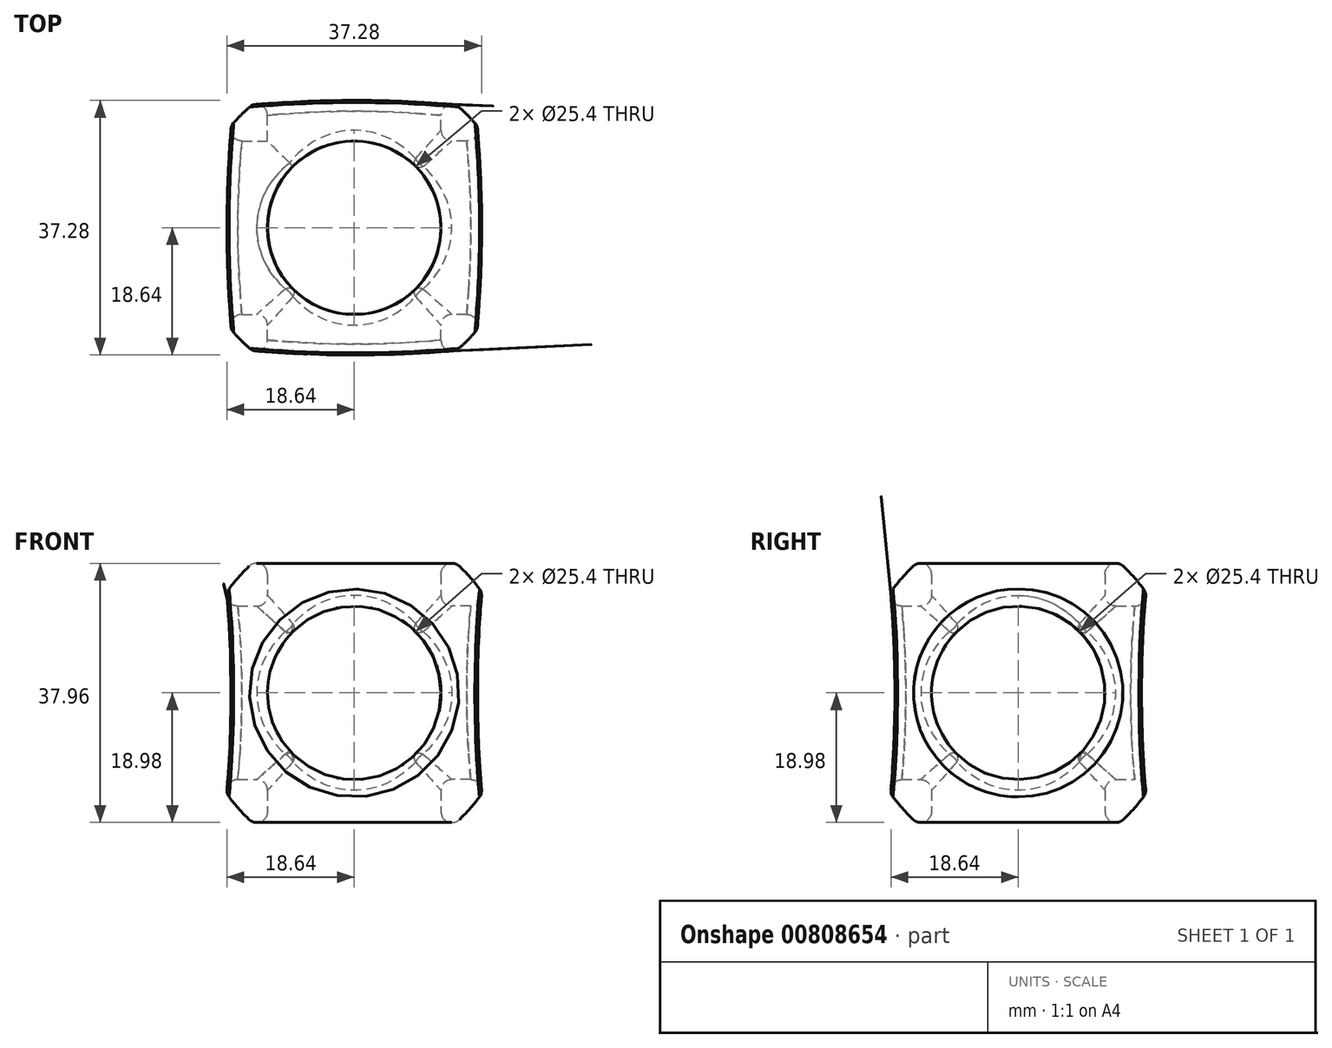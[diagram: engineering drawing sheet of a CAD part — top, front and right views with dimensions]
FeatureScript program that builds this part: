
annotation { "Feature Type Name" : "Feature", "Feature Type Description" : "" }
export const myFeature = defineFeature(function(context is Context, id is Id, definition is map)
    precondition{}
    {
        {
            var Q0;
            Q0=qCreatedBy(makeId("Front.planeOp"),FACE);
            var sketch = newSketch(context, id + "F0", { "sketchPlane" : qUnion([Q0])});
            skLineSegment(sketch, "E0", {"start": v(0, 0) * mm, "end": v(0, 50.8) * mm});
            skArc(sketch, "E1", {"start": v(0, 50.8) * mm, "mid": v(-23.38, 25.4) * mm, "end": v(0, 0) * mm});
            skSolve(sketch);
        }
        {
            var Q0;
            Q0=makeQuery(id+"F0.imprint","IMPRINT",FACE,{"disambiguationData":[TD([[makeQuery(id+"F0.imprint","IMPRINT",EDGE,{"derivedFrom":sQuery(id+"F0.wireOp",EDGE,"E0")}),1.0]])]});
            var Q1;
            Q1=sQuery(id+"F0.wireOp",EDGE,"E0");
            revolve(context, id + "F1", {"surfaceOperationType" : NewSurfaceOperationType.NEW, "entities" : qUnion([Q0]), "axis" : qUnion([Q1]), "revolveType" : RevolveType.FULL});
        }
        {
            var Q0;
            Q0=qCreatedBy(makeId("Top.planeOp"),FACE);
            var sketch = newSketch(context, id + "F2", { "sketchPlane" : qUnion([Q0])});
            skCircle(sketch, "E2", {"center": v(0, 0) * mm, "radius": 12.7 * mm});
            skSolve(sketch);
        }
        {
            var Q0;
            Q0=makeQuery(id+"F2.imprint","IMPRINT",FACE,{"disambiguationData":[TD([[makeQuery(id+"F2.imprint","IMPRINT",EDGE,{"derivedFrom":sQuery(id+"F2.wireOp",EDGE,"E2")}),1.0]])]});
            extrude(context, id + "F3", {"entities" : qUnion([Q0]), "operationType" : NewBodyOperationType.REMOVE, "endBound" : BoundingType.THROUGH_ALL, "depth" : 25.4 * mm, "offsetDistance" : 25.4 * mm});
        }
        {
            var Q0;
            Q0=qCreatedBy(makeId("Right.planeOp"),FACE);
            var sketch = newSketch(context, id + "F4", { "sketchPlane" : qUnion([Q0])});
            skCircle(sketch, "E3", {"center": v(0, 25.4) * mm, "radius": 12.7 * mm});
            skSolve(sketch);
        }
        {
            var Q0;
            Q0 = qSketchRegion(id + "F4", true);
            extrude(context, id + "F5", {"entities" : qUnion([Q0]), "operationType" : NewBodyOperationType.REMOVE, "endBound" : BoundingType.THROUGH_ALL, "oppositeDirection" : true, "depth" : 25.4 * mm, "offsetDistance" : 25.4 * mm});
        }
        {
            var Q0;
            Q0 = qSketchRegion(id + "F4", true);
            extrude(context, id + "F6", {"entities" : qUnion([Q0]), "operationType" : NewBodyOperationType.REMOVE, "depth" : 25.4 * mm, "offsetDistance" : 25.4 * mm});
        }
        {
            var Q0;
            Q0=qCreatedBy(makeId("Front.planeOp"),FACE);
            var sketch = newSketch(context, id + "F7", { "sketchPlane" : qUnion([Q0])});
            skPoint(sketch, "E4", {"position": v(0, 25.4) * mm});
            skCircle(sketch, "E5", {"center": v(0, 25.4) * mm, "radius": 12.7 * mm});
            skSolve(sketch);
        }
        {
            var Q0;
            Q0=makeQuery(id+"F7.imprint","IMPRINT",FACE,{"disambiguationData":[TD([[makeQuery(id+"F7.imprint","IMPRINT",EDGE,{"derivedFrom":sQuery(id+"F7.wireOp",EDGE,"E5")}),1.0]])]});
            extrude(context, id + "F8", {"entities" : qUnion([Q0]), "operationType" : NewBodyOperationType.REMOVE, "endBound" : BoundingType.THROUGH_ALL, "depth" : 25.4 * mm, "offsetDistance" : 25.4 * mm, "hasSecondDirection" : true, "secondDirectionOppositeDirection" : true, "secondDirectionDepth" : 25.4 * mm});
        }
        {
            var Q0;
            Q0=makeQuery(id+"F3.boolean.opBoolean","INTERSECT",EDGE,{"disambiguationData":[OD(1.0)],"derivedFrom":[makeQuery(id+"F1.opRevolve","SWEPT_FACE",FACE,{"disambiguationData":[OSD([sQuery(id+"F0.wireOp",EDGE,"E1")])]}),makeQuery(id+"F3.opExtrude","SWEPT_FACE",FACE,{"disambiguationData":[OSD([sQuery(id+"F2.wireOp",EDGE,"E2")])]})]});
            var Q1;
            Q1=makeQuery(id+"F8.boolean.opBoolean","INTERSECT",EDGE,{"disambiguationData":[OD(0.0)],"derivedFrom":[makeQuery(id+"F1.opRevolve","SWEPT_FACE",FACE,{"disambiguationData":[OSD([sQuery(id+"F0.wireOp",EDGE,"E1")])]}),makeQuery(id+"F8.opExtrude","SWEPT_FACE",FACE,{"disambiguationData":[OSD([sQuery(id+"F7.wireOp",EDGE,"E5")])]})]});
            var Q2;
            Q2=makeQuery(id+"F6.boolean.opBoolean","INTERSECT",EDGE,{"derivedFrom":[makeQuery(id+"F1.opRevolve","SWEPT_FACE",FACE,{"disambiguationData":[OSD([sQuery(id+"F0.wireOp",EDGE,"E1")])]}),makeQuery(id+"F6.opExtrude","SWEPT_FACE",FACE,{"disambiguationData":[OSD([sQuery(id+"F4.wireOp",EDGE,"E3")])]})]});
            var Q3;
            Q3=makeQuery(id+"F8.boolean.opBoolean","INTERSECT",EDGE,{"disambiguationData":[OD(1.0)],"derivedFrom":[makeQuery(id+"F1.opRevolve","SWEPT_FACE",FACE,{"disambiguationData":[OSD([sQuery(id+"F0.wireOp",EDGE,"E1")])]}),makeQuery(id+"F8.opExtrude","SWEPT_FACE",FACE,{"disambiguationData":[OSD([sQuery(id+"F7.wireOp",EDGE,"E5")])]})]});
            var Q4;
            Q4=makeQuery(id+"F5.boolean.opBoolean","INTERSECT",EDGE,{"derivedFrom":[makeQuery(id+"F1.opRevolve","SWEPT_FACE",FACE,{"disambiguationData":[OSD([sQuery(id+"F0.wireOp",EDGE,"E1")])]}),makeQuery(id+"F5.opExtrude","SWEPT_FACE",FACE,{"disambiguationData":[OSD([sQuery(id+"F4.wireOp",EDGE,"E3")])]})]});
            var Q5;
            Q5=makeQuery(id+"F3.boolean.opBoolean","INTERSECT",EDGE,{"disambiguationData":[OD(0.0)],"derivedFrom":[makeQuery(id+"F1.opRevolve","SWEPT_FACE",FACE,{"disambiguationData":[OSD([sQuery(id+"F0.wireOp",EDGE,"E1")])]}),makeQuery(id+"F3.opExtrude","SWEPT_FACE",FACE,{"disambiguationData":[OSD([sQuery(id+"F2.wireOp",EDGE,"E2")])]})]});
            var Q6;
            Q6=makeQuery(id+"F6.boolean.opBoolean","INTERSECT",EDGE,{"disambiguationData":[OD(1.0)],"derivedFrom":[makeQuery(id+"F3.boolean.opBoolean","COPY",FACE,{"derivedFrom":makeQuery(id+"F3.opExtrude","SWEPT_FACE",FACE,{"disambiguationData":[OSD([sQuery(id+"F2.wireOp",EDGE,"E2")])]})}),makeQuery(id+"F6.opExtrude","SWEPT_FACE",FACE,{"disambiguationData":[OSD([sQuery(id+"F4.wireOp",EDGE,"E3")])]})]});
            var Q7;
            Q7=makeQuery(id+"F8.boolean.opBoolean","INTERSECT",EDGE,{"disambiguationData":[OD(1.0)],"derivedFrom":[makeQuery(id+"F6.boolean.opBoolean","COPY",FACE,{"derivedFrom":makeQuery(id+"F6.opExtrude","SWEPT_FACE",FACE,{"disambiguationData":[OSD([sQuery(id+"F4.wireOp",EDGE,"E3")])]})}),makeQuery(id+"F8.opExtrude","SWEPT_FACE",FACE,{"disambiguationData":[OSD([sQuery(id+"F7.wireOp",EDGE,"E5")])]})]});
            var Q8;
            Q8=makeQuery(id+"F8.boolean.opBoolean","INTERSECT",EDGE,{"disambiguationData":[OD(1.0)],"derivedFrom":[makeQuery(id+"F6.boolean.opBoolean","SPLIT",FACE,{"disambiguationData":[OD(1.0)],"derivedFrom":makeQuery(id+"F3.boolean.opBoolean","COPY",FACE,{"derivedFrom":makeQuery(id+"F3.opExtrude","SWEPT_FACE",FACE,{"disambiguationData":[OSD([sQuery(id+"F2.wireOp",EDGE,"E2")])]})})}),makeQuery(id+"F8.opExtrude","SWEPT_FACE",FACE,{"disambiguationData":[OSD([sQuery(id+"F7.wireOp",EDGE,"E5")])]})]});
            var Q9;
            Q9=makeQuery(id+"F8.boolean.opBoolean","INTERSECT",EDGE,{"disambiguationData":[OD(0.0)],"derivedFrom":[makeQuery(id+"F6.boolean.opBoolean","SPLIT",FACE,{"disambiguationData":[OD(1.0)],"derivedFrom":makeQuery(id+"F3.boolean.opBoolean","COPY",FACE,{"derivedFrom":makeQuery(id+"F3.opExtrude","SWEPT_FACE",FACE,{"disambiguationData":[OSD([sQuery(id+"F2.wireOp",EDGE,"E2")])]})})}),makeQuery(id+"F8.opExtrude","SWEPT_FACE",FACE,{"disambiguationData":[OSD([sQuery(id+"F7.wireOp",EDGE,"E5")])]})]});
            var Q10;
            Q10=makeQuery(id+"F8.boolean.opBoolean","INTERSECT",EDGE,{"disambiguationData":[OD(0.0)],"derivedFrom":[makeQuery(id+"F6.boolean.opBoolean","COPY",FACE,{"derivedFrom":makeQuery(id+"F6.opExtrude","SWEPT_FACE",FACE,{"disambiguationData":[OSD([sQuery(id+"F4.wireOp",EDGE,"E3")])]})}),makeQuery(id+"F8.opExtrude","SWEPT_FACE",FACE,{"disambiguationData":[OSD([sQuery(id+"F7.wireOp",EDGE,"E5")])]})]});
            var Q11;
            Q11=makeQuery(id+"F8.boolean.opBoolean","INTERSECT",EDGE,{"disambiguationData":[OD(0.0)],"derivedFrom":[makeQuery(id+"F5.boolean.opBoolean","COPY",FACE,{"derivedFrom":makeQuery(id+"F5.opExtrude","SWEPT_FACE",FACE,{"disambiguationData":[OSD([sQuery(id+"F4.wireOp",EDGE,"E3")])]})}),makeQuery(id+"F8.opExtrude","SWEPT_FACE",FACE,{"disambiguationData":[OSD([sQuery(id+"F7.wireOp",EDGE,"E5")])]})]});
            var Q12;
            Q12=makeQuery(id+"F8.boolean.opBoolean","INTERSECT",EDGE,{"disambiguationData":[OD(0.0)],"derivedFrom":[makeQuery(id+"F6.boolean.opBoolean","SPLIT",FACE,{"disambiguationData":[OD(0.0)],"derivedFrom":makeQuery(id+"F3.boolean.opBoolean","COPY",FACE,{"derivedFrom":makeQuery(id+"F3.opExtrude","SWEPT_FACE",FACE,{"disambiguationData":[OSD([sQuery(id+"F2.wireOp",EDGE,"E2")])]})})}),makeQuery(id+"F8.opExtrude","SWEPT_FACE",FACE,{"disambiguationData":[OSD([sQuery(id+"F7.wireOp",EDGE,"E5")])]})]});
            var Q13;
            Q13=makeQuery(id+"F5.boolean.opBoolean","INTERSECT",EDGE,{"disambiguationData":[OD(0.0)],"derivedFrom":[makeQuery(id+"F3.boolean.opBoolean","COPY",FACE,{"derivedFrom":makeQuery(id+"F3.opExtrude","SWEPT_FACE",FACE,{"disambiguationData":[OSD([sQuery(id+"F2.wireOp",EDGE,"E2")])]})}),makeQuery(id+"F5.opExtrude","SWEPT_FACE",FACE,{"disambiguationData":[OSD([sQuery(id+"F4.wireOp",EDGE,"E3")])]})]});
            var Q14;
            Q14=makeQuery(id+"F5.boolean.opBoolean","INTERSECT",EDGE,{"disambiguationData":[OD(1.0)],"derivedFrom":[makeQuery(id+"F3.boolean.opBoolean","COPY",FACE,{"derivedFrom":makeQuery(id+"F3.opExtrude","SWEPT_FACE",FACE,{"disambiguationData":[OSD([sQuery(id+"F2.wireOp",EDGE,"E2")])]})}),makeQuery(id+"F5.opExtrude","SWEPT_FACE",FACE,{"disambiguationData":[OSD([sQuery(id+"F4.wireOp",EDGE,"E3")])]})]});
            var Q15;
            Q15=makeQuery(id+"F8.boolean.opBoolean","INTERSECT",EDGE,{"disambiguationData":[OD(1.0)],"derivedFrom":[makeQuery(id+"F6.boolean.opBoolean","SPLIT",FACE,{"disambiguationData":[OD(0.0)],"derivedFrom":makeQuery(id+"F3.boolean.opBoolean","COPY",FACE,{"derivedFrom":makeQuery(id+"F3.opExtrude","SWEPT_FACE",FACE,{"disambiguationData":[OSD([sQuery(id+"F2.wireOp",EDGE,"E2")])]})})}),makeQuery(id+"F8.opExtrude","SWEPT_FACE",FACE,{"disambiguationData":[OSD([sQuery(id+"F7.wireOp",EDGE,"E5")])]})]});
            var Q16;
            Q16=makeQuery(id+"F6.boolean.opBoolean","INTERSECT",EDGE,{"disambiguationData":[OD(0.0)],"derivedFrom":[makeQuery(id+"F3.boolean.opBoolean","COPY",FACE,{"derivedFrom":makeQuery(id+"F3.opExtrude","SWEPT_FACE",FACE,{"disambiguationData":[OSD([sQuery(id+"F2.wireOp",EDGE,"E2")])]})}),makeQuery(id+"F6.opExtrude","SWEPT_FACE",FACE,{"disambiguationData":[OSD([sQuery(id+"F4.wireOp",EDGE,"E3")])]})]});
            fillet(context, id + "F9", {"entities" : qUnion([Q0, Q1, Q2, Q3, Q4, Q5, Q6, Q7, Q8, Q9, Q10, Q11, Q12, Q13, Q14, Q15, Q16]), "radius" : 1.59 * mm, "tangentPropagation" : true, "allowEdgeOverflow" : false});
        }
    });
